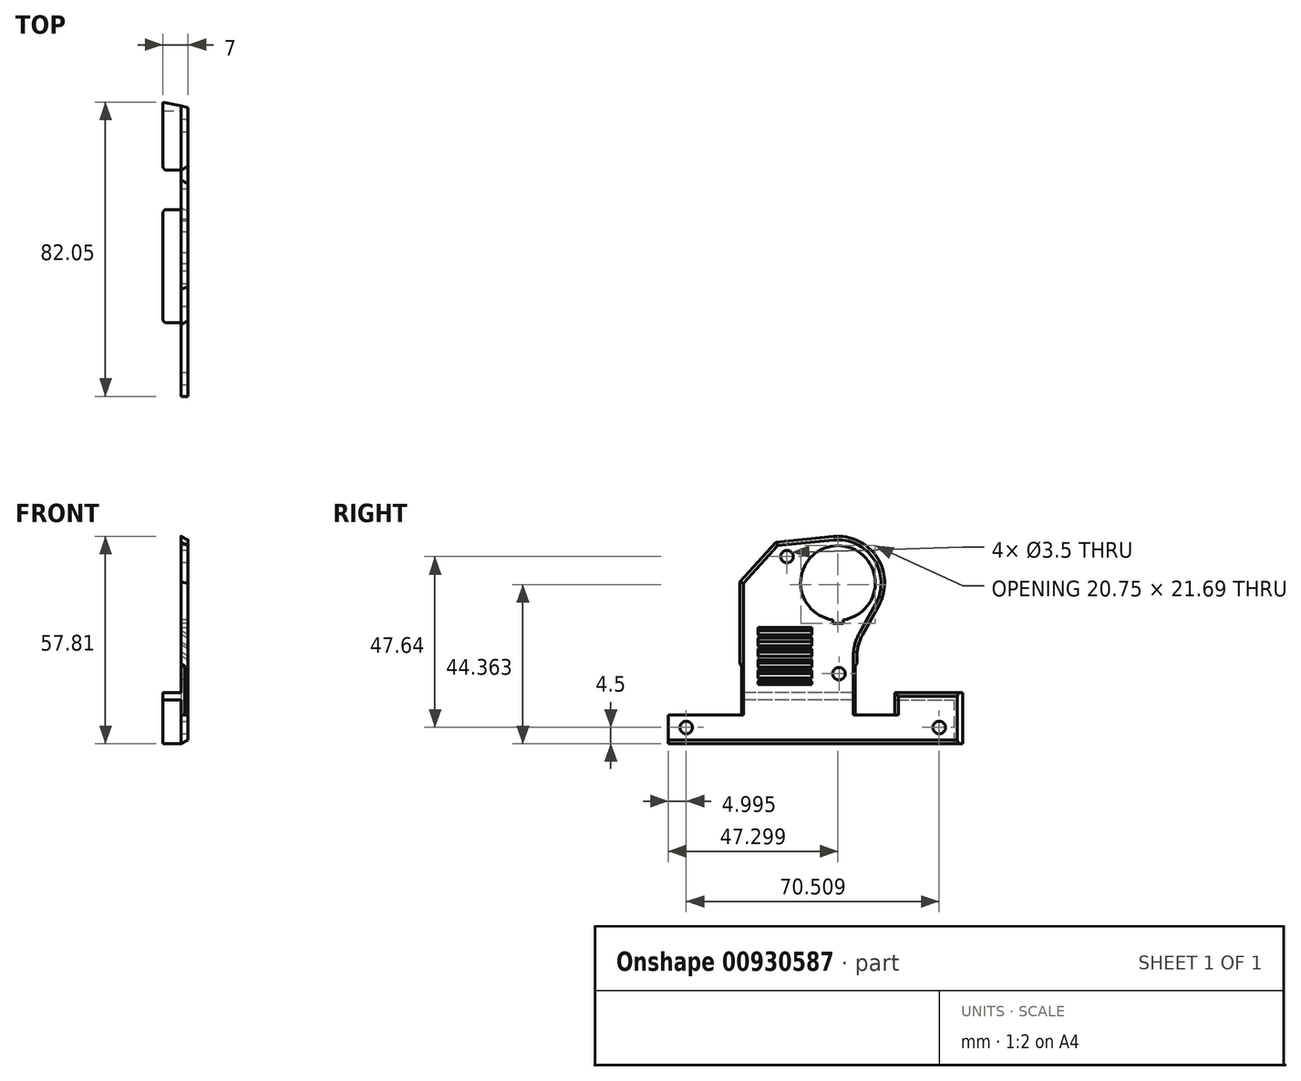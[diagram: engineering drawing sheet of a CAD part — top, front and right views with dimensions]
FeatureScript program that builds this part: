
annotation { "Feature Type Name" : "Feature", "Feature Type Description" : "" }
export const myFeature = defineFeature(function(context is Context, id is Id, definition is map)
    precondition{}
    {
        {
            var Q0;
            Q0=qCreatedBy(makeId("Right.planeOp"),FACE);
            var sketch = newSketch(context, id + "F0", { "sketchPlane" : qUnion([Q0])});
            skLineSegment(sketch, "E0", {"start": v(-91.61, 41.95) * mm, "end": v(-91.61, 0) * mm, "construction": true});
            skLineSegment(sketch, "E1", {"start": v(-91.61, 0) * mm, "end": v(0, 0) * mm, "construction": true});
            skLineSegment(sketch, "E2", {"start": v(0, 0) * mm, "end": v(0, 35.08) * mm, "construction": true});
            skLineSegment(sketch, "E3", {"start": v(0, 35.08) * mm, "end": v(-31.78, 47.96) * mm, "construction": true});
            skLineSegment(sketch, "E4", {"start": v(-91.61, 41.95) * mm, "end": v(-31.78, 47.96) * mm, "construction": true});
            skLineSegment(sketch, "E5.top", {"start": v(-81.61, -5.5) * mm, "end": v(-61.61, -5.5) * mm, "construction": true});
            skLineSegment(sketch, "E5.left", {"start": v(-81.61, 0) * mm, "end": v(-81.61, -5.5) * mm, "construction": true});
            skLineSegment(sketch, "E5.right", {"start": v(-61.61, 0) * mm, "end": v(-61.61, -5.5) * mm, "construction": true});
            skLineSegment(sketch, "E6.top", {"start": v(-29.03, -5.5) * mm, "end": v(-19.03, -5.5) * mm, "construction": true});
            skLineSegment(sketch, "E6.left", {"start": v(-29.03, 0) * mm, "end": v(-29.03, -5.5) * mm, "construction": true});
            skLineSegment(sketch, "E6.right", {"start": v(-19.03, 0) * mm, "end": v(-19.03, -5.5) * mm, "construction": true});
            skLineSegment(sketch, "E7", {"start": v(-91.61, 0) * mm, "end": v(-91.61, -3) * mm, "construction": true});
            skLineSegment(sketch, "E8", {"start": v(-91.61, -3) * mm, "end": v(-81.61, -3) * mm, "construction": true});
            skLineSegment(sketch, "E9", {"start": v(-61.61, -3) * mm, "end": v(-29.03, -3) * mm, "construction": true});
            skLineSegment(sketch, "E10", {"start": v(0, 0) * mm, "end": v(0, -3) * mm, "construction": true});
            skLineSegment(sketch, "E11", {"start": v(0, -3) * mm, "end": v(-19.03, -3) * mm, "construction": true});
            skLineSegment(sketch, "E12", {"start": v(-91.61, 13) * mm, "end": v(0, 13) * mm, "construction": true});
            skLineSegment(sketch, "E13", {"start": v(-91.61, 10) * mm, "end": v(0, 10) * mm, "construction": true});
            skLineSegment(sketch, "E14", {"start": v(-81.61, 0) * mm, "end": v(-81.61, 2) * mm, "construction": true});
            skLineSegment(sketch, "E15", {"start": v(-81.61, 2) * mm, "end": v(-61.61, 2) * mm, "construction": true});
            skLineSegment(sketch, "E16", {"start": v(-61.61, 2) * mm, "end": v(-61.61, 0) * mm, "construction": true});
            skLineSegment(sketch, "E17", {"start": v(-29.03, 0) * mm, "end": v(-29.03, 2) * mm, "construction": true});
            skLineSegment(sketch, "E18", {"start": v(-29.03, 2) * mm, "end": v(-19.03, 2) * mm, "construction": true});
            skLineSegment(sketch, "E19", {"start": v(-19.03, 2) * mm, "end": v(-19.03, 0) * mm, "construction": true});
            skSolve(sketch);
        }
        {
            var Q0;
            Q0=qCreatedBy(makeId("Right.planeOp"),FACE);
            var sketch = newSketch(context, id + "F1", { "sketchPlane" : qUnion([Q0])});
            skLineSegment(sketch, "E20", {"start": v(0, -14.5) * mm, "end": v(-81.61, -14.5) * mm});
            skLineSegment(sketch, "E21", {"start": v(-81.61, -14.5) * mm, "end": v(-81.61, -6.5) * mm});
            skLineSegment(sketch, "E22", {"start": v(-81.61, -6.5) * mm, "end": v(-61.11, -6.5) * mm});
            skLineSegment(sketch, "E23", {"start": v(0, -0.3) * mm, "end": v(0, -14.5) * mm});
            skCircle(sketch, "E24", {"center": v(-34.31, 30.3) * mm, "radius": 10.1 * mm, "construction": true});
            skLineSegment(sketch, "E25", {"start": v(-29.53, 7.04) * mm, "end": v(-29.53, -6.5) * mm});
            skLineSegment(sketch, "E26", {"start": v(-34.31, 30.3) * mm, "end": v(-34.31, 13) * mm, "construction": true});
            skLineSegment(sketch, "E27", {"start": v(-34.31, 30.3) * mm, "end": v(-36.04, 47.53) * mm, "construction": true});
            skLineSegment(sketch, "E28", {"start": v(-34.31, 30.3) * mm, "end": v(-27.8, 46.35) * mm, "construction": true});
            skArc(sketch, "E29", {"start": v(-22.94, 24.02) * mm, "mid": v(-23.46, 37.46) * mm, "end": v(-35.61, 43.24) * mm});
            skArc(sketch, "E30", {"start": v(-32.81, 20.02) * mm, "mid": v(-34.31, 40.7) * mm, "end": v(-35.81, 20.02) * mm});
            skLineSegment(sketch, "E31", {"start": v(-35.81, 20.02) * mm, "end": v(-35.81, 19.02) * mm});
            skLineSegment(sketch, "E32", {"start": v(-35.81, 19.02) * mm, "end": v(-32.81, 19.02) * mm});
            skLineSegment(sketch, "E33", {"start": v(-32.81, 19.02) * mm, "end": v(-32.81, 20.02) * mm});
            skLineSegment(sketch, "E34", {"start": v(-27.53, 15.71) * mm, "end": v(-22.94, 24.02) * mm});
            skLineSegment(sketch, "E35", {"start": v(-35.61, 43.24) * mm, "end": v(-51.67, 41.63) * mm});
            skArc(sketch, "E36", {"start": v(-35.61, 43.24) * mm, "mid": v(-45.16, 23.15) * mm, "end": v(-22.94, 24.02) * mm, "construction": true});
            skLineSegment(sketch, "E37", {"start": v(-61.61, 30.63) * mm, "end": v(-61.61, 8) * mm});
            skLineSegment(sketch, "E38", {"start": v(0, -0.3) * mm, "end": v(-18.53, -0.3) * mm});
            skLineSegment(sketch, "E39", {"start": v(-18.53, -0.3) * mm, "end": v(-18.53, -6.5) * mm});
            skLineSegment(sketch, "E40", {"start": v(-18.53, -6.5) * mm, "end": v(-29.53, -6.5) * mm});
            skLineSegment(sketch, "E41", {"start": v(-61.61, 30.63) * mm, "end": v(-51.67, 41.63) * mm});
            skPoint(sketch, "E42.orphan", {"position": v(-61.61, 40.63) * mm});
            skLineSegment(sketch, "E43", {"start": v(-29.03, -6.5) * mm, "end": v(-29.03, 9.9) * mm, "construction": true});
            skPoint(sketch, "E44.visualSharp", {"position": v(-29.03, 13) * mm});
            skArc(sketch, "E44.filletArc", {"start": v(-27.53, 15.71) * mm, "mid": v(-28.65, 12.9) * mm, "end": v(-29.03, 9.9) * mm});
            skLineSegment(sketch, "E45", {"start": v(-29.03, 9.9) * mm, "end": v(-29.03, 7.9) * mm});
            skLineSegment(sketch, "E46", {"start": v(-29.03, 7.9) * mm, "end": v(-29.53, 7.04) * mm});
            skCircle(sketch, "E47", {"center": v(-48.53, 37.64) * mm, "radius": 1.75 * mm});
            skCircle(sketch, "E48", {"center": v(-34.03, 5) * mm, "radius": 1.75 * mm});
            skCircle(sketch, "E49", {"center": v(-34.31, 30.3) * mm, "radius": 11 * mm, "construction": true});
            skLineSegment(sketch, "E50", {"start": v(-48.53, 37.64) * mm, "end": v(-52.24, 41) * mm, "construction": true});
            skLineSegment(sketch, "E51", {"start": v(-48.53, 37.64) * mm, "end": v(-44.09, 35.35) * mm, "construction": true});
            skLineSegment(sketch, "E52", {"start": v(-44.09, 35.35) * mm, "end": v(-34.31, 30.3) * mm, "construction": true});
            skLineSegment(sketch, "E53", {"start": v(-61.61, 8) * mm, "end": v(-61.11, 7.13) * mm});
            skLineSegment(sketch, "E54", {"start": v(-61.11, 7.13) * mm, "end": v(-61.11, -6.5) * mm});
            skSolve(sketch);
        }
        {
            var Q0;
            Q0=qSketchRegion(id+"F1",true);
            extrude(context, id + "F2", {"entities" : qUnion([Q0]), "depth" : 2 * mm, "offsetDistance" : 25 * mm});
        }
        {
            var Q0;
            Q0=makeQuery(id+"F2.opExtrude","CAP_EDGE",EDGE,{"disambiguationData":[OSD([sQuery(id+"F1.wireOp",EDGE,"E41")])],"isStart":false});
            var Q1;
            Q1=makeQuery(id+"F2.opExtrude","CAP_EDGE",EDGE,{"disambiguationData":[OSD([sQuery(id+"F1.wireOp",EDGE,"E35")])],"isStart":false});
            var Q2;
            Q2=makeQuery(id+"F2.opExtrude","CAP_EDGE",EDGE,{"disambiguationData":[OSD([sQuery(id+"F1.wireOp",EDGE,"E39")])],"isStart":false});
            var Q3;
            Q3=makeQuery(id+"F2.opExtrude","CAP_EDGE",EDGE,{"disambiguationData":[OSD([sQuery(id+"F1.wireOp",EDGE,"E38")])],"isStart":false});
            chamfer(context, id + "F3", {"entities" : qUnion([Q0, Q1, Q2, Q3]), "chamferType" : ChamferType.TWO_OFFSETS, "width1" : 2 * mm, "oppositeDirection" : false, "width2" : 1 * mm, "tangentPropagation" : true});
        }
        {
            var Q0;
            Q0=makeQuery(id+"F2.opExtrude","SWEPT_FACE",FACE,{"disambiguationData":[OSD([sQuery(id+"F1.wireOp",EDGE,"E22")])]});
            var sketch = newSketch(context, id + "F4", { "sketchPlane" : qUnion([Q0])});
            skLineSegment(sketch, "E55", {"start": v(0, -61.61) * mm, "end": v(2, -60.61) * mm});
            skLineSegment(sketch, "E56", {"start": v(2, -60.61) * mm, "end": v(2, -61.61) * mm});
            skLineSegment(sketch, "E57", {"start": v(2, -61.61) * mm, "end": v(0, -61.61) * mm});
            skSolve(sketch);
        }
        {
            var Q0;
            Q0=qSketchRegion(id+"F4",true);
            var Q1;
            Q1=makeQuery(id+"F3.opChamfer","BLEND_FACE",FACE,{"disambiguationData":[OSD([sQuery(id+"F1.wireOp",EDGE,"E41")])]});
            extrude(context, id + "F5", {"entities" : qUnion([Q0]), "operationType" : NewBodyOperationType.REMOVE, "endBound" : BoundingType.UP_TO_SURFACE, "depth" : 25 * mm, "endBoundEntityFace" : qUnion([Q1]), "offsetDistance" : 25 * mm});
        }
        {
            var Q0;
            Q0=makeQuery(id+"F2.opExtrude","CAP_FACE",FACE,{"disambiguationData":[OSD([sQuery(id+"F1.wireOp",EDGE,"E20"),sQuery(id+"F1.wireOp",EDGE,"E21"),sQuery(id+"F1.wireOp",EDGE,"E22"),sQuery(id+"F1.wireOp",EDGE,"E23"),sQuery(id+"F1.wireOp",EDGE,"E25"),sQuery(id+"F1.wireOp",EDGE,"E29"),sQuery(id+"F1.wireOp",EDGE,"E30"),sQuery(id+"F1.wireOp",EDGE,"E31"),sQuery(id+"F1.wireOp",EDGE,"E32"),sQuery(id+"F1.wireOp",EDGE,"E33"),sQuery(id+"F1.wireOp",EDGE,"E34"),sQuery(id+"F1.wireOp",EDGE,"E35"),sQuery(id+"F1.wireOp",EDGE,"E37"),sQuery(id+"F1.wireOp",EDGE,"E38"),sQuery(id+"F1.wireOp",EDGE,"E39"),sQuery(id+"F1.wireOp",EDGE,"E40"),sQuery(id+"F1.wireOp",EDGE,"E41"),sQuery(id+"F1.wireOp",EDGE,"E44.filletArc"),sQuery(id+"F1.wireOp",EDGE,"E45"),sQuery(id+"F1.wireOp",EDGE,"E46"),sQuery(id+"F1.wireOp",EDGE,"E47"),sQuery(id+"F1.wireOp",EDGE,"E48")])],"isStart":true});
            var sketch = newSketch(context, id + "F6", { "sketchPlane" : qUnion([Q0])});
            skLineSegment(sketch, "E58", {"start": v(0, -0.3) * mm, "end": v(18.53, -0.3) * mm});
            skLineSegment(sketch, "E59", {"start": v(18.53, -0.3) * mm, "end": v(18.53, -2.3) * mm});
            skLineSegment(sketch, "E60", {"start": v(18.53, -2.3) * mm, "end": v(2, -2.3) * mm});
            skLineSegment(sketch, "E61", {"start": v(2, -2.3) * mm, "end": v(2, -14.5) * mm});
            skLineSegment(sketch, "E62", {"start": v(2, -14.5) * mm, "end": v(0, -14.5) * mm});
            skLineSegment(sketch, "E63", {"start": v(0, -14.5) * mm, "end": v(0, -0.3) * mm});
            skSolve(sketch);
        }
        {
            var Q0;
            Q0=qSketchRegion(id+"F6",true);
            extrude(context, id + "F7", {"entities" : qUnion([Q0]), "operationType" : NewBodyOperationType.ADD, "depth" : 5 * mm, "offsetDistance" : 25 * mm});
        }
        {
            var Q0;
            Q0=makeQuery(id+"F7.opExtrude","SWEPT_FACE",FACE,{"disambiguationData":[OSD([sQuery(id+"F6.wireOp",EDGE,"E58")])]});
            var sketch = newSketch(context, id + "F8", { "sketchPlane" : qUnion([Q0])});
            skLineSegment(sketch, "E64", {"start": v(2, -1.1) * mm, "end": v(2, 0) * mm});
            skLineSegment(sketch, "E65", {"start": v(-3, 0) * mm, "end": v(-3, -18.53) * mm, "construction": true});
            skLineSegment(sketch, "E66", {"start": v(-3, 0) * mm, "end": v(2, -1.1) * mm});
            skLineSegment(sketch, "E67", {"start": v(-3, 0) * mm, "end": v(2, 0) * mm});
            skSolve(sketch);
        }
        {
            var Q0;
            Q0=qSketchRegion(id+"F8",true);
            var Q1;
            Q1=makeQuery(id+"F7.opExtrude","SWEPT_FACE",FACE,{"disambiguationData":[OSD([sQuery(id+"F6.wireOp",EDGE,"E62")])]});
            extrude(context, id + "F9", {"entities" : qUnion([Q0]), "operationType" : NewBodyOperationType.REMOVE, "endBound" : BoundingType.UP_TO_SURFACE, "oppositeDirection" : true, "depth" : 25 * mm, "endBoundEntityFace" : qUnion([Q1]), "offsetDistance" : 25 * mm});
        }
        {
            var Q0;
            Q0=makeQuery(id+"F7.opExtrude","SWEPT_FACE",FACE,{"disambiguationData":[OSD([sQuery(id+"F6.wireOp",EDGE,"E58")])]});
            var sketch = newSketch(context, id + "F10", { "sketchPlane" : qUnion([Q0])});
            skLineSegment(sketch, "E68", {"start": v(-3, 0) * mm, "end": v(-5, 0.44) * mm});
            skLineSegment(sketch, "E69", {"start": v(-5, 0.44) * mm, "end": v(-5, 0) * mm});
            skLineSegment(sketch, "E70", {"start": v(-5, 0) * mm, "end": v(-3, 0) * mm});
            skSolve(sketch);
        }
        {
            var Q0;
            Q0=qSketchRegion(id+"F10",true);
            var Q1;
            Q1=makeQuery(id+"F7.opExtrude","SWEPT_FACE",FACE,{"disambiguationData":[OSD([sQuery(id+"F6.wireOp",EDGE,"E62")])]});
            extrude(context, id + "F11", {"entities" : qUnion([Q0]), "operationType" : NewBodyOperationType.ADD, "endBound" : BoundingType.UP_TO_SURFACE, "oppositeDirection" : true, "depth" : 25 * mm, "endBoundEntityFace" : qUnion([Q1]), "offsetDistance" : 25 * mm});
        }
        {
            var Q0;
            Q0=makeQuery(id+"F2.opExtrude","CAP_FACE",FACE,{"disambiguationData":[OSD([sQuery(id+"F1.wireOp",EDGE,"E20"),sQuery(id+"F1.wireOp",EDGE,"E21"),sQuery(id+"F1.wireOp",EDGE,"E22"),sQuery(id+"F1.wireOp",EDGE,"E23"),sQuery(id+"F1.wireOp",EDGE,"E25"),sQuery(id+"F1.wireOp",EDGE,"E29"),sQuery(id+"F1.wireOp",EDGE,"E30"),sQuery(id+"F1.wireOp",EDGE,"E31"),sQuery(id+"F1.wireOp",EDGE,"E32"),sQuery(id+"F1.wireOp",EDGE,"E33"),sQuery(id+"F1.wireOp",EDGE,"E34"),sQuery(id+"F1.wireOp",EDGE,"E35"),sQuery(id+"F1.wireOp",EDGE,"E37"),sQuery(id+"F1.wireOp",EDGE,"E38"),sQuery(id+"F1.wireOp",EDGE,"E39"),sQuery(id+"F1.wireOp",EDGE,"E40"),sQuery(id+"F1.wireOp",EDGE,"E41"),sQuery(id+"F1.wireOp",EDGE,"E44.filletArc"),sQuery(id+"F1.wireOp",EDGE,"E45"),sQuery(id+"F1.wireOp",EDGE,"E46"),sQuery(id+"F1.wireOp",EDGE,"E47"),sQuery(id+"F1.wireOp",EDGE,"E48")])],"isStart":true});
            var sketch = newSketch(context, id + "F12", { "sketchPlane" : qUnion([Q0])});
            skLineSegment(sketch, "E71", {"start": v(29.53, -0.3) * mm, "end": v(61.11, -0.3) * mm});
            skLineSegment(sketch, "E72", {"start": v(29.53, -0.3) * mm, "end": v(29.53, -2.3) * mm});
            skLineSegment(sketch, "E73", {"start": v(29.53, -2.3) * mm, "end": v(61.11, -2.3) * mm});
            skLineSegment(sketch, "E74", {"start": v(61.11, -2.3) * mm, "end": v(61.11, -0.3) * mm});
            skSolve(sketch);
        }
        {
            var Q0;
            Q0=qSketchRegion(id+"F12",true);
            extrude(context, id + "F13", {"entities" : qUnion([Q0]), "operationType" : NewBodyOperationType.ADD, "depth" : 1 * mm, "offsetDistance" : 25 * mm});
        }
        {
            var Q0;
            Q0=makeQuery(id+"F2.opExtrude","CAP_EDGE",EDGE,{"disambiguationData":[OSD([sQuery(id+"F1.wireOp",EDGE,"E20")])],"isStart":false});
            chamfer(context, id + "F14", {"entities" : qUnion([Q0]), "chamferType" : ChamferType.TWO_OFFSETS, "width1" : 2 * mm, "oppositeDirection" : false, "width2" : 1 * mm, "tangentPropagation" : true});
        }
        {
            var Q0;
            Q0=makeQuery(id+"F2.opExtrude","CAP_FACE",FACE,{"disambiguationData":[OSD([sQuery(id+"F1.wireOp",EDGE,"E20"),sQuery(id+"F1.wireOp",EDGE,"E21"),sQuery(id+"F1.wireOp",EDGE,"E22"),sQuery(id+"F1.wireOp",EDGE,"E23"),sQuery(id+"F1.wireOp",EDGE,"E25"),sQuery(id+"F1.wireOp",EDGE,"E29"),sQuery(id+"F1.wireOp",EDGE,"E30"),sQuery(id+"F1.wireOp",EDGE,"E31"),sQuery(id+"F1.wireOp",EDGE,"E32"),sQuery(id+"F1.wireOp",EDGE,"E33"),sQuery(id+"F1.wireOp",EDGE,"E34"),sQuery(id+"F1.wireOp",EDGE,"E35"),sQuery(id+"F1.wireOp",EDGE,"E37"),sQuery(id+"F1.wireOp",EDGE,"E38"),sQuery(id+"F1.wireOp",EDGE,"E39"),sQuery(id+"F1.wireOp",EDGE,"E40"),sQuery(id+"F1.wireOp",EDGE,"E41"),sQuery(id+"F1.wireOp",EDGE,"E44.filletArc"),sQuery(id+"F1.wireOp",EDGE,"E45"),sQuery(id+"F1.wireOp",EDGE,"E46"),sQuery(id+"F1.wireOp",EDGE,"E47"),sQuery(id+"F1.wireOp",EDGE,"E48")])],"isStart":false});
            var sketch = newSketch(context, id + "F15", { "sketchPlane" : qUnion([Q0])});
            skCircle(sketch, "E75", {"center": v(-76.61, -10) * mm, "radius": 1.75 * mm});
            skCircle(sketch, "E76", {"center": v(-6.1, -10) * mm, "radius": 1.75 * mm});
            skLineSegment(sketch, "E77", {"start": v(-76.61, -10) * mm, "end": v(-6.1, -10) * mm, "construction": true});
            skSolve(sketch);
        }
        {
            var Q0;
            Q0=qSketchRegion(id+"F15",true);
            extrude(context, id + "F16", {"entities" : qUnion([Q0]), "operationType" : NewBodyOperationType.REMOVE, "endBound" : BoundingType.UP_TO_NEXT, "oppositeDirection" : true, "depth" : 25 * mm, "offsetDistance" : 25 * mm});
        }
        {
            var Q0;
            Q0=makeQuery(id+"F13.opExtrude","CAP_FACE",FACE,{"disambiguationData":[OSD([sQuery(id+"F12.wireOp",EDGE,"cqBWEjJI-844c-Ycew-BMv1-GbYCSaLPAW9f"),sQuery(id+"F12.wireOp",EDGE,"u2vOaJZC-jWlj-LDpC-TzX2-33LMqBNMJH1q"),sQuery(id+"F12.wireOp",EDGE,"TYdgHHg5-SBbf-GiLz-N15G-Su78sUBprq7P"),sQuery(id+"F12.wireOp",EDGE,"mxjitm2S-s73c-T2P9-recr-LieKxJWPdM18"),sQuery(id+"F12.wireOp",EDGE,"Dq8brY0R-sAHm-DFA5-6tZW-h0nVSSd7ZLRs"),sQuery(id+"F12.wireOp",EDGE,"6sKBBNcE-AKpc-RuOe-tWiS-tXF6T1XBfiL4"),sQuery(id+"F12.wireOp",EDGE,"eJvgXfSe-M3EK-J6gp-fCzT-rjfZv0GaCMWH"),sQuery(id+"F12.wireOp",EDGE,"368CWHds-0VaT-ZemY-tOJ5-psSm9oLhfdzX"),sQuery(id+"F12.wireOp",EDGE,"pyVk9kSB-A0Jr-QfkN-WJ3Z-bRQPsDTPnTn4"),sQuery(id+"F12.wireOp",EDGE,"E71"),sQuery(id+"F12.wireOp",EDGE,"E72"),sQuery(id+"F12.wireOp",EDGE,"E73"),sQuery(id+"F12.wireOp",EDGE,"E74"),sQuery(id+"F12.wireOp",EDGE,"T5IVG7mr-GRrJ-tOb7-7o0p-XzpdBMSTo0RD")])],"isStart":false});
            var sketch = newSketch(context, id + "F17", { "sketchPlane" : qUnion([Q0])});
            skLineSegment(sketch, "E78.bottom", {"start": v(29.53, -0.3) * mm, "end": v(61.11, -0.3) * mm});
            skLineSegment(sketch, "E78.top", {"start": v(29.53, -2.3) * mm, "end": v(61.11, -2.3) * mm});
            skLineSegment(sketch, "E78.left", {"start": v(29.53, -0.3) * mm, "end": v(29.53, -2.3) * mm});
            skLineSegment(sketch, "E78.right", {"start": v(61.11, -0.3) * mm, "end": v(61.11, -2.3) * mm});
            skSolve(sketch);
        }
        {
            var Q0;
            Q0=qSketchRegion(id+"F17",true);
            extrude(context, id + "F18", {"entities" : qUnion([Q0]), "operationType" : NewBodyOperationType.ADD, "depth" : 4 * mm, "offsetDistance" : 25 * mm});
        }
        {
            var Q0;
            Q0=makeQuery(id+"F7.opExtrude","CAP_EDGE",EDGE,{"disambiguationData":[OSD([sQuery(id+"F6.wireOp",EDGE,"E59")])],"isStart":false});
            var Q1;
            Q1=makeQuery(id+"F18.opExtrude","CAP_EDGE",EDGE,{"disambiguationData":[OSD([sQuery(id+"F17.wireOp",EDGE,"E78.left")])],"isStart":false});
            var Q2;
            Q2=makeQuery(id+"F18.opExtrude","CAP_EDGE",EDGE,{"disambiguationData":[OSD([sQuery(id+"F17.wireOp",EDGE,"E78.right")])],"isStart":false});
            fillet(context, id + "F19", {"entities" : qUnion([Q0, Q1, Q2]), "radius" : 1 * mm, "tangentPropagation" : true, "allowEdgeOverflow" : false});
        }
        {
            var Q0;
            Q0=makeQuery(id+"F2.opExtrude","CAP_FACE",FACE,{"disambiguationData":[OSD([sQuery(id+"F1.wireOp",EDGE,"E20"),sQuery(id+"F1.wireOp",EDGE,"E21"),sQuery(id+"F1.wireOp",EDGE,"E22"),sQuery(id+"F1.wireOp",EDGE,"E23"),sQuery(id+"F1.wireOp",EDGE,"E25"),sQuery(id+"F1.wireOp",EDGE,"E29"),sQuery(id+"F1.wireOp",EDGE,"E30"),sQuery(id+"F1.wireOp",EDGE,"E31"),sQuery(id+"F1.wireOp",EDGE,"E32"),sQuery(id+"F1.wireOp",EDGE,"E33"),sQuery(id+"F1.wireOp",EDGE,"E34"),sQuery(id+"F1.wireOp",EDGE,"E35"),sQuery(id+"F1.wireOp",EDGE,"E37"),sQuery(id+"F1.wireOp",EDGE,"E38"),sQuery(id+"F1.wireOp",EDGE,"E39"),sQuery(id+"F1.wireOp",EDGE,"E40"),sQuery(id+"F1.wireOp",EDGE,"E41"),sQuery(id+"F1.wireOp",EDGE,"E44.filletArc"),sQuery(id+"F1.wireOp",EDGE,"E45"),sQuery(id+"F1.wireOp",EDGE,"E46"),sQuery(id+"F1.wireOp",EDGE,"E47"),sQuery(id+"F1.wireOp",EDGE,"E48"),sQuery(id+"F1.wireOp",EDGE,"E53"),sQuery(id+"F1.wireOp",EDGE,"E54")])],"isStart":false});
            var sketch = newSketch(context, id + "F20", { "sketchPlane" : qUnion([Q0])});
            skLineSegment(sketch, "E79.bottom", {"start": v(-56.61, 17.9) * mm, "end": v(-41.61, 17.9) * mm});
            skLineSegment(sketch, "E79.top", {"start": v(-56.61, 2) * mm, "end": v(-41.61, 2) * mm});
            skLineSegment(sketch, "E79.left", {"start": v(-56.61, 17.9) * mm, "end": v(-56.61, 2) * mm});
            skLineSegment(sketch, "E79.right", {"start": v(-41.61, 17.9) * mm, "end": v(-41.61, 2) * mm});
            skSolve(sketch);
        }
        {
            var Q0;
            Q0=qSketchRegion(id+"F20",true);
            extrude(context, id + "F21", {"entities" : qUnion([Q0]), "operationType" : NewBodyOperationType.REMOVE, "endBound" : BoundingType.UP_TO_NEXT, "oppositeDirection" : true, "depth" : 25 * mm, "offsetDistance" : 25 * mm});
        }
        {
            var Q0;
            Q0=makeQuery(id+"F21.boolean.opBoolean","COPY",FACE,{"derivedFrom":makeQuery(id+"F21.opExtrude","SWEPT_FACE",FACE,{"disambiguationData":[OSD([sQuery(id+"F20.wireOp",EDGE,"E79.right")])]})});
            var sketch = newSketch(context, id + "F22", { "sketchPlane" : qUnion([Q0])});
            skLineSegment(sketch, "E80", {"start": v(1, 17.9) * mm, "end": v(1, 2) * mm, "construction": true});
            skLineSegment(sketch, "E81", {"start": v(2, 9.95) * mm, "end": v(0, 9.95) * mm, "construction": true});
            skLineSegment(sketch, "E82", {"start": v(2, 8.9) * mm, "end": v(2, 9.83) * mm});
            skLineSegment(sketch, "E83", {"start": v(2, 9.83) * mm, "end": v(0, 10.99) * mm});
            skLineSegment(sketch, "E84", {"start": v(0, 10.99) * mm, "end": v(0, 10.06) * mm});
            skLineSegment(sketch, "E85", {"start": v(0, 10.06) * mm, "end": v(2, 8.9) * mm});
            skLineSegment(sketch, "E86", {"start": v(0, 10.53) * mm, "end": v(2, 9.37) * mm, "construction": true});
            skLineSegment(sketch, "E87", {"start": v(2, 9.95) * mm, "end": v(2, 9.83) * mm, "construction": true});
            skLineSegment(sketch, "E88", {"start": v(0, 9.95) * mm, "end": v(0, 10.06) * mm, "construction": true});
            skLineSegment(sketch, "E89", {"start": v(2, 11.91) * mm, "end": v(0, 13.07) * mm});
            skLineSegment(sketch, "E90", {"start": v(0, 13.07) * mm, "end": v(0, 14) * mm});
            skLineSegment(sketch, "E91", {"start": v(0, 14) * mm, "end": v(2, 12.84) * mm});
            skLineSegment(sketch, "E92", {"start": v(2, 12.84) * mm, "end": v(2, 11.91) * mm});
            skLineSegment(sketch, "E93", {"start": v(2, 14.91) * mm, "end": v(2, 15.84) * mm});
            skLineSegment(sketch, "E94", {"start": v(2, 15.84) * mm, "end": v(0, 17) * mm});
            skLineSegment(sketch, "E95", {"start": v(0, 17) * mm, "end": v(0, 16.07) * mm});
            skLineSegment(sketch, "E96", {"start": v(0, 16.07) * mm, "end": v(2, 14.91) * mm});
            skLineSegment(sketch, "E97", {"start": v(0, 7.99) * mm, "end": v(2, 6.83) * mm});
            skLineSegment(sketch, "E98", {"start": v(2, 6.83) * mm, "end": v(2, 5.9) * mm});
            skLineSegment(sketch, "E99", {"start": v(2, 5.9) * mm, "end": v(0, 7.06) * mm});
            skLineSegment(sketch, "E100", {"start": v(0, 7.06) * mm, "end": v(0, 7.99) * mm});
            skLineSegment(sketch, "E101", {"start": v(2, 3.83) * mm, "end": v(2, 2.9) * mm});
            skLineSegment(sketch, "E102", {"start": v(2, 2.9) * mm, "end": v(0, 4.06) * mm});
            skLineSegment(sketch, "E103", {"start": v(0, 4.06) * mm, "end": v(0, 4.98) * mm});
            skLineSegment(sketch, "E104", {"start": v(0, 4.98) * mm, "end": v(2, 3.83) * mm});
            skSolve(sketch);
        }
        {
            var Q0;
            Q0=qSketchRegion(id+"F22",true);
            extrude(context, id + "F23", {"entities" : qUnion([Q0]), "operationType" : NewBodyOperationType.ADD, "depth" : 15 * mm, "offsetDistance" : 25 * mm});
        }
    });
